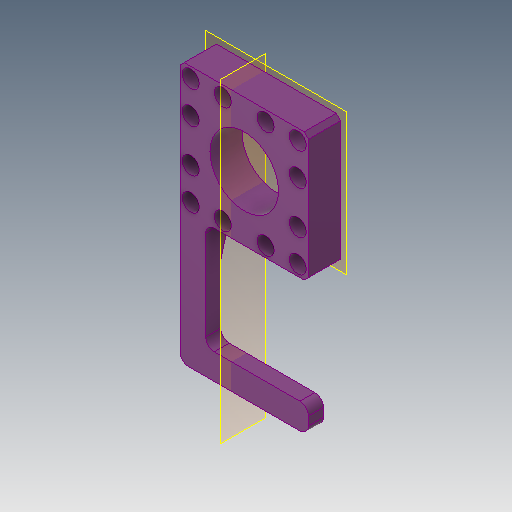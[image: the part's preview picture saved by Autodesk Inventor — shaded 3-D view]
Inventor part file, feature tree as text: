
AUTODESK INVENTOR PART (.ipt)
format: ipt  version: 2019.4 (Build 234330000, 330)  size: 255,488 bytes
history: native  units: mm
features: other x6, extrude x4, reference x4, sketch x3, plane x2, projected_geometry x2, fillet x1, hole x1, chamfer x1
ambient origin geometry x8: Origin, YZ Plane, XZ Plane, XY Plane, X Axis, Y Axis, Z Axis, Center Point
bodies: Solid1 (feature_tree)
feature tree (24):
  plane  "Work Plane1"
  extrude  "Extrusion1"  Depth=7.0mm TaperAngle=0.0deg
  extrude  "Extrusion2"  Depth=4.0mm
  fillet  "Fillet1"  Radius=4.0mm
  extrude  "Extrusion6"  Depth=12.0mm
  plane  "Work Plane2"
  hole  "Hole1"  [1 undecoded]
  extrude  "Extrusion7"  Depth=12.0mm
  chamfer  "Chamfer3"  Distance=5.0mm Angle=75.0deg
  reference  "Reference1"
  reference  "Reference2"
  projected_geometry  "Projected Loop1"
  sketch  "Sketch6"  dims[d1=8.0mm d2=0.0mm d6=7.0mm d7=0.0mm]
  projected_geometry  "Projected Loop5"
  reference  "Reference4"
  sketch  "Sketch7"  dims[d12=4.0mm d27=4.9mm d28=4.0mm d29=0.0mm]
  reference  "Reference5"
  sketch  "Sketch8"  dims[d31=3.2mm d32=6.0mm d33=8.0mm d34=10.0mm d35=90.0deg d36=8.0mm d37=20.594885mm d41=32.0mm d42=4.0mm d43=0.0mm d59=12.0mm d60=5.0mm d61=2.0mm d62=75.0deg d77=12.0mm]
  other  "Application_Fluorescence_Microscope_Infinity_cellstorm_v3.iam"
  other  "00_XY_stage-CHUO_SEIKI_LD-647-R1:1"
  other  "00_XY_stage-CHUO_SEIKI_LD-647-R1-Top:1"
  other  "00_Microscope_Objective:1"
  other  "cellSTORM_UC2_Sample.iam"
  other  "cellSTORM_inverted_chiptray_v0:1"
note: 1 required parameter value undecoded (feature->parameter linkage not recoverable at this tier; creation-order binding heuristic only, values carry confidence <= 0.55)
